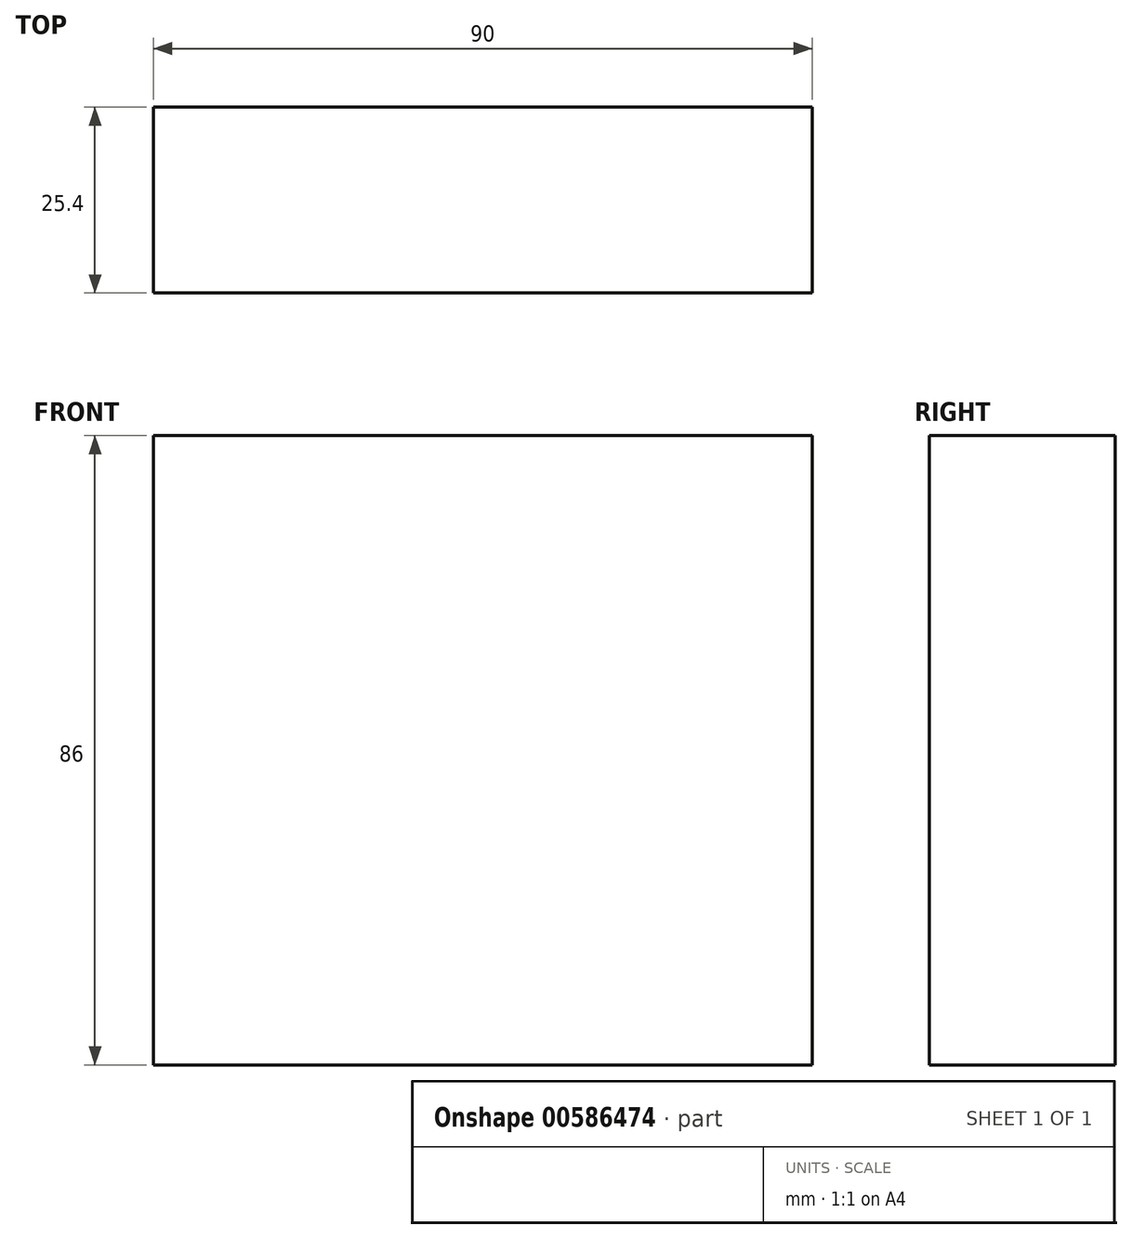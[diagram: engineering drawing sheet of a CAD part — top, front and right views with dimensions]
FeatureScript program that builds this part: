
annotation { "Feature Type Name" : "Feature", "Feature Type Description" : "" }
export const myFeature = defineFeature(function(context is Context, id is Id, definition is map)
    precondition{}
    {
        {
            var Q0;
            Q0=qCreatedBy(makeId("Front.planeOp"),FACE);
            var sketch = newSketch(context, id + "F0", { "sketchPlane" : qUnion([Q0])});
            skLineSegment(sketch, "E0.bottom", {"start": v(-45, 43) * mm, "end": v(45, 43) * mm});
            skLineSegment(sketch, "E0.top", {"start": v(-45, -43) * mm, "end": v(45, -43) * mm});
            skLineSegment(sketch, "E0.left", {"start": v(-45, 43) * mm, "end": v(-45, -43) * mm});
            skLineSegment(sketch, "E0.right", {"start": v(45, 43) * mm, "end": v(45, -43) * mm});
            skPoint(sketch, "E0.middle", {"position": v(0, 0) * mm});
            skSolve(sketch);
        }
        {
            var Q0;
            Q0=makeQuery(id+"F0.imprint","IMPRINT",FACE,{"disambiguationData":[TD([[makeQuery(id+"F0.imprint","IMPRINT",EDGE,{"derivedFrom":sQuery(id+"F0.wireOp",EDGE,"E0.bottom")}),-1.0]])]});
            extrude(context, id + "F1", {"entities" : qUnion([Q0]), "endBound" : BoundingType.SYMMETRIC, "depth" : 25.4 * mm, "offsetDistance" : 25.4 * mm});
        }
    });
